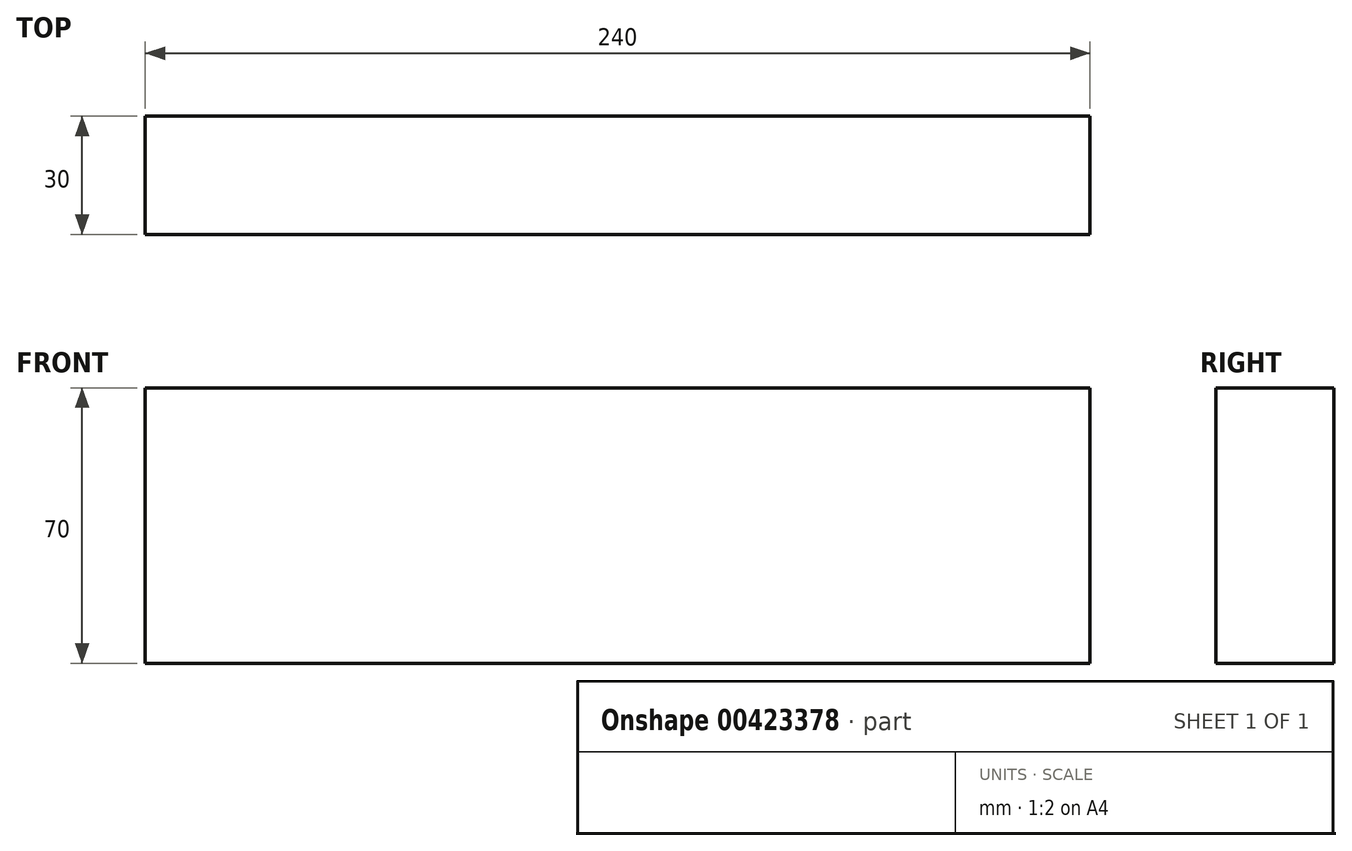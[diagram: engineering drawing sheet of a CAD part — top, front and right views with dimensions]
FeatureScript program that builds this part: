
annotation { "Feature Type Name" : "Feature", "Feature Type Description" : "" }
export const myFeature = defineFeature(function(context is Context, id is Id, definition is map)
    precondition{}
    {
        {
            var Q0;
            Q0=qCreatedBy(makeId("Front.planeOp"),FACE);
            var sketch = newSketch(context, id + "F0", { "sketchPlane" : qUnion([Q0])});
            skLineSegment(sketch, "E0.bottom", {"start": v(182.08, 36.26) * mm, "end": v(-57.92, 36.26) * mm});
            skLineSegment(sketch, "E0.top", {"start": v(182.08, -33.74) * mm, "end": v(-57.92, -33.74) * mm});
            skLineSegment(sketch, "E0.left", {"start": v(182.08, 36.26) * mm, "end": v(182.08, -33.74) * mm});
            skLineSegment(sketch, "E0.right", {"start": v(-57.92, 36.26) * mm, "end": v(-57.92, -33.74) * mm});
            skSolve(sketch);
        }
        {
            var Q0;
            Q0=makeQuery(id+"F0.imprint","IMPRINT",FACE,{"disambiguationData":[TD([[makeQuery(id+"F0.imprint","IMPRINT",EDGE,{"derivedFrom":sQuery(id+"F0.wireOp",EDGE,"E0.bottom")}),1.0]])]});
            extrude(context, id + "F1", {"entities" : qUnion([Q0]), "depth" : 30 * mm});
        }
    });
